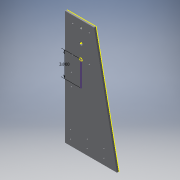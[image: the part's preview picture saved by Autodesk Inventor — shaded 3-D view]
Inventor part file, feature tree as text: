
AUTODESK INVENTOR PART (.ipt)
format: ipt  version: 2016 (Build 200138000, 138)  size: 171,520 bytes
history: native  units: in
note: dims shown in document units (in); Inventor stores cm internally (conversion verified against a paired STEP export)
features: sketch x6, extrude x4, reference x2, projected_geometry x2, plane x1
ambient origin geometry x8: Origin, YZ Plane, XZ Plane, XY Plane, X Axis, Y Axis, Z Axis, Center Point
bodies: Solid1 (feature_tree)
feature tree (15):
  plane  "Work Plane1"
  extrude  "Extrusion1"  Depth=0.5in
  extrude  "Extrusion2"  Depth=0.24in TaperAngle=0.0deg
  extrude  "Extrusion3"  Depth=13.75in
  sketch  "Sketch4"  dims[d11=0.5in d12=1.0in]
  sketch  "Sketch5"  dims[d13=0.175in]
  extrude  "Extrusion4"  Depth=1.0in
  sketch  "Sketch1"  dims[d0=0.414in d1=0.5in]
  reference  "Reference1"
  sketch  "Sketch2"  dims[d4=3.5in d6=0.24in d7=0.0in]
  reference  "Reference2"
  sketch  "Sketch3"  dims[d8=1.0in d9=0.0in d10=13.75in]
  projected_geometry  "Projected Loop1"
  projected_geometry  "Projected Loop2"
  sketch  "Sketch6"  dims[d14=0.175in d15=0.175in d16=0.175in d17=0.175in d18=0.175in d19=1.0in d20=0.0in d21=3.0in d22=6.0in d23=0.75in d24=1.5in d25=0.175in d26=0.175in d27=1.0in d28=0.0in]
